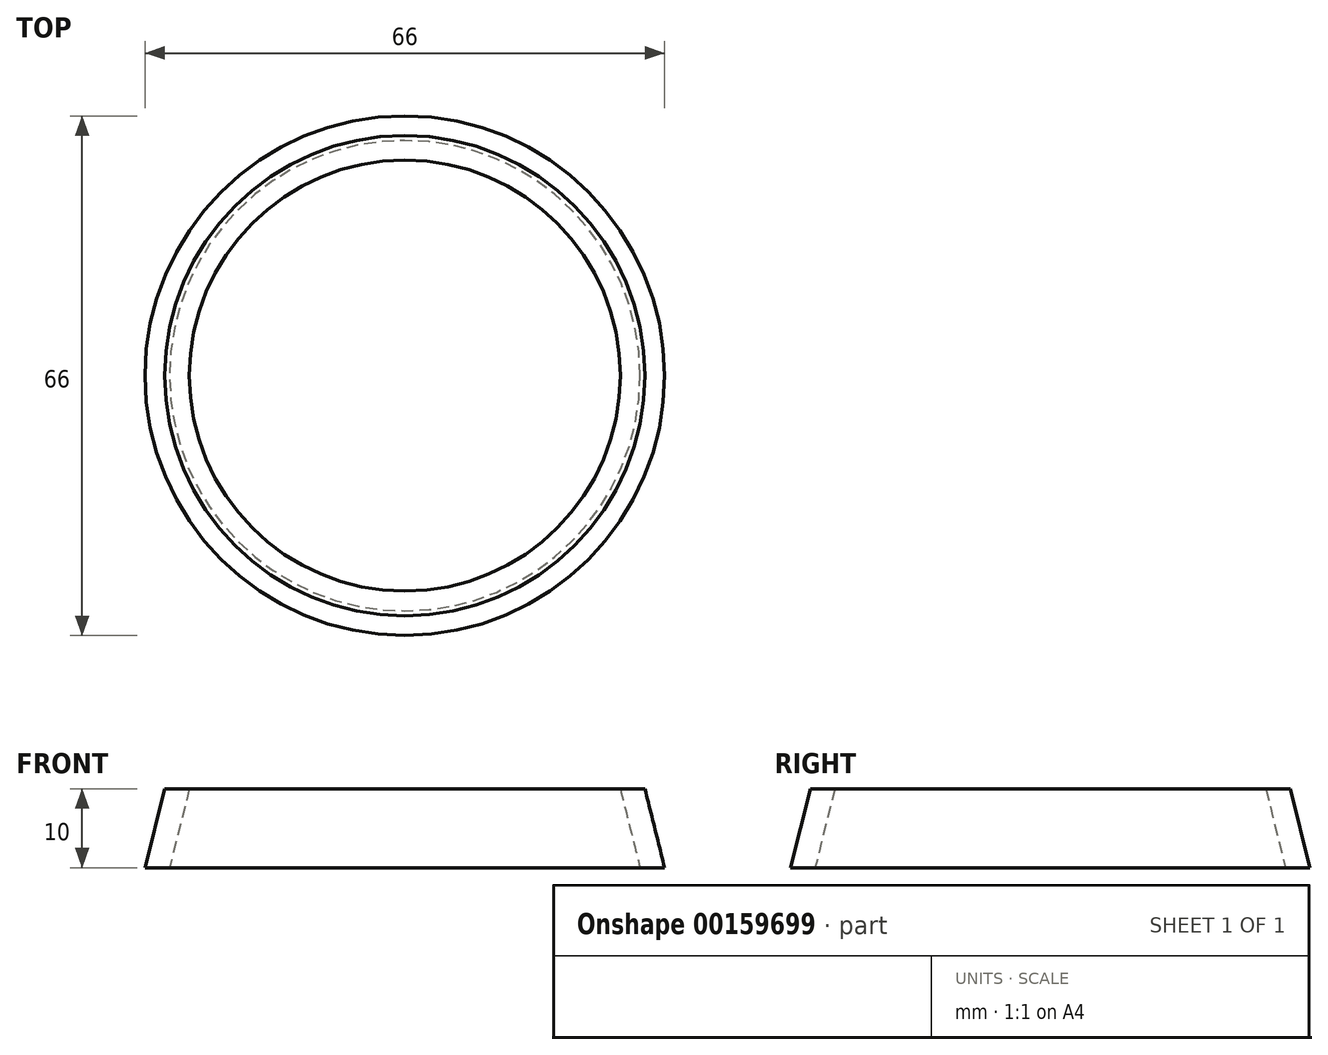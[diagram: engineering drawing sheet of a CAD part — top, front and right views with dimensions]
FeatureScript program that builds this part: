
annotation { "Feature Type Name" : "Feature", "Feature Type Description" : "" }
export const myFeature = defineFeature(function(context is Context, id is Id, definition is map)
    precondition{}
    {
        {
            var Q0;
            Q0=qCreatedBy(makeId("Top.planeOp"),FACE);
            var sketch = newSketch(context, id + "F0", { "sketchPlane" : qUnion([Q0])});
            skCircle(sketch, "E0", {"center": v(0, 0) * mm, "radius": 27.38 * mm});
            skSolve(sketch);
        }
        {
            var Q0;
            Q0=qCreatedBy(makeId("Top.planeOp"),FACE);
            var sketch = newSketch(context, id + "F1", { "sketchPlane" : qUnion([Q0])});
            skCircle(sketch, "E1", {"center": v(0, 0) * mm, "radius": 30.5 * mm});
            skSolve(sketch);
        }
        {
            var Q0;
            Q0=qCreatedBy(makeId("Top.planeOp"),FACE);
            cPlane(context, id + "F2", {"entities" : qUnion([Q0]), "cplaneType" : CPlaneType.OFFSET, "offset" : 10 * mm, "oppositeDirection" : true, "width" : 150 * mm, "height" : 150 * mm});
        }
        {
            var Q0;
            Q0=qCreatedBy(id+"F2.planeOp",FACE);
            var sketch = newSketch(context, id + "F3", { "sketchPlane" : qUnion([Q0])});
            skCircle(sketch, "E2", {"center": v(0, 0) * mm, "radius": 29.88 * mm});
            skSolve(sketch);
        }
        {
            var Q0;
            Q0=qCreatedBy(id+"F2.planeOp",FACE);
            var sketch = newSketch(context, id + "F4", { "sketchPlane" : qUnion([Q0])});
            skCircle(sketch, "E3.0", {"center": v(0, 0) * mm, "radius": 33 * mm});
            skSolve(sketch);
        }
        {
            var Q0;
            Q0=makeQuery(id+"F4.imprint","IMPRINT",FACE,{"disambiguationData":[TD([[makeQuery(id+"F4.imprint","IMPRINT",EDGE,{"derivedFrom":sQuery(id+"F4.wireOp",EDGE,"E3.0")}),1.0]])]});
            var Q1;
            Q1=makeQuery(id+"F1.imprint","IMPRINT",FACE,{"disambiguationData":[TD([[makeQuery(id+"F1.imprint","IMPRINT",EDGE,{"derivedFrom":sQuery(id+"F1.wireOp",EDGE,"E1")}),1.0]])]});
            loft(context, id + "F5", {"sheetProfilesArray" : [{ "sheetProfileEntities" : qUnion([Q0]) }, { "sheetProfileEntities" : qUnion([Q1]) }]});
        }
        {
            var Q0;
            Q0=makeQuery(id+"F3.imprint","IMPRINT",FACE,{"disambiguationData":[TD([[makeQuery(id+"F3.imprint","IMPRINT",EDGE,{"derivedFrom":sQuery(id+"F3.wireOp",EDGE,"E2")}),1.0]])]});
            var Q1;
            Q1=qSketchRegion(id+"F0",true);
            loft(context, id + "F6", {"operationType" : NewBodyOperationType.REMOVE, "sheetProfilesArray" : [{ "sheetProfileEntities" : qUnion([Q0]) }, { "sheetProfileEntities" : qUnion([Q1]) }]});
        }
    });
